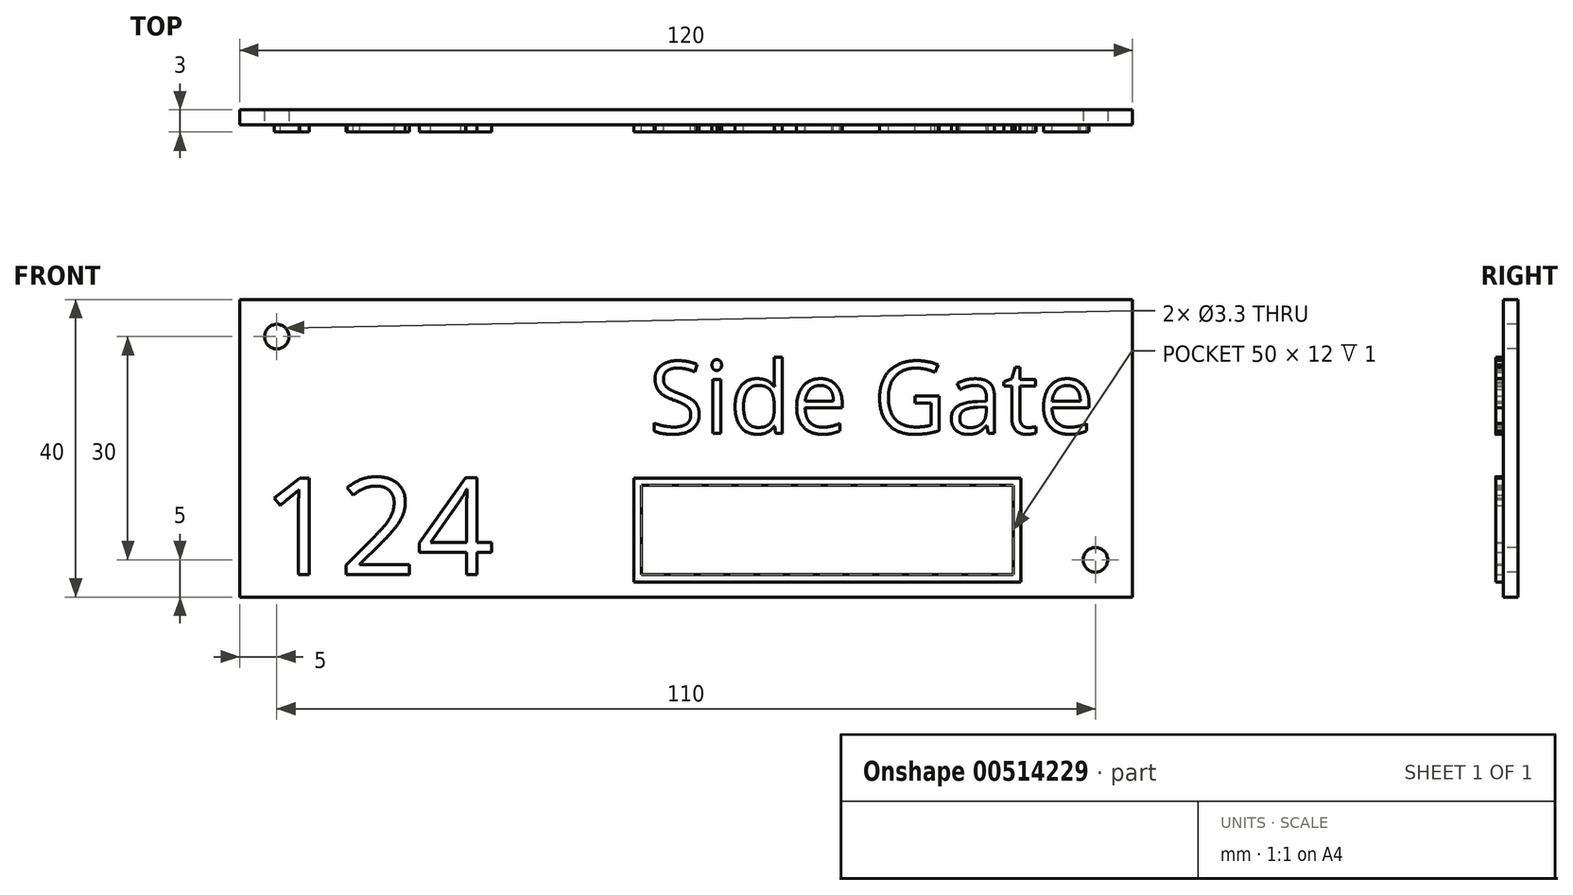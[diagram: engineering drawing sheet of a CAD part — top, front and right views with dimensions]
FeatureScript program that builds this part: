
annotation { "Feature Type Name" : "Feature", "Feature Type Description" : "" }
export const myFeature = defineFeature(function(context is Context, id is Id, definition is map)
    precondition{}
    {
        {
            var Q0;
            Q0=qCreatedBy(makeId("Front.planeOp"),FACE);
            var sketch = newSketch(context, id + "F0", { "sketchPlane" : qUnion([Q0])});
            skLineSegment(sketch, "E0.bottom", {"start": v(60, -20) * mm, "end": v(-60, -20) * mm});
            skLineSegment(sketch, "E0.top", {"start": v(60, 20) * mm, "end": v(-60, 20) * mm});
            skLineSegment(sketch, "E0.left", {"start": v(60, -20) * mm, "end": v(60, 20) * mm});
            skLineSegment(sketch, "E0.right", {"start": v(-60, -20) * mm, "end": v(-60, 20) * mm});
            skPoint(sketch, "E0.middle", {"position": v(0, 0) * mm});
            skSolve(sketch);
        }
        {
            var Q0;
            Q0=makeQuery(id+"F0.imprint","IMPRINT",FACE,{"disambiguationData":[TD([[makeQuery(id+"F0.imprint","IMPRINT",EDGE,{"derivedFrom":sQuery(id+"F0.wireOp",EDGE,"E0.bottom")}),-1.0]])]});
            extrude(context, id + "F1", {"entities" : qUnion([Q0]), "depth" : 2 * mm});
        }
        {
            var Q0;
            Q0=makeQuery(id+"F1.opExtrude","CAP_FACE",FACE,{"disambiguationData":[OSD([sQuery(id+"F0.wireOp",EDGE,"E0.bottom"),sQuery(id+"F0.wireOp",EDGE,"E0.top"),sQuery(id+"F0.wireOp",EDGE,"E0.left"),sQuery(id+"F0.wireOp",EDGE,"E0.right")])],"isStart":false});
            var sketch = newSketch(context, id + "F2", { "sketchPlane" : qUnion([Q0])});
            skPoint(sketch, "E1", {"position": v(-55, 15) * mm});
            skPoint(sketch, "E2", {"position": v(55, -15) * mm});
            skSolve(sketch);
        }
        {
            var Q0;
            Q0=sQuery(id+"F2.wireOp",VERTEX,"E1");
            var Q1;
            Q1=sQuery(id+"F2.wireOp",VERTEX,"E2");
            var Q2;
            Q2=makeQuery(id+"F1.opExtrude","SWEPT_BODY",BODY,{"disambiguationData":[OSD([sQuery(id+"F0.wireOp",EDGE,"E0.bottom"),sQuery(id+"F0.wireOp",EDGE,"E0.top"),sQuery(id+"F0.wireOp",EDGE,"E0.left"),sQuery(id+"F0.wireOp",EDGE,"E0.right")])]});
            hole(context, id + "F3", {"style" : HoleStyle.SIMPLE, "endStyle" : HoleEndStyle.THROUGH, "holeDiameter" : 3.3 * mm, "locations" : qUnion([Q0, Q1]), "scope" : qUnion([Q2]), "isTappedThrough" : true});
        }
        {
            var Q0;
            Q0=makeQuery(id+"F1.opExtrude","CAP_FACE",FACE,{"disambiguationData":[OSD([sQuery(id+"F0.wireOp",EDGE,"E0.bottom"),sQuery(id+"F0.wireOp",EDGE,"E0.top"),sQuery(id+"F0.wireOp",EDGE,"E0.left"),sQuery(id+"F0.wireOp",EDGE,"E0.right")])],"isStart":false});
            var sketch = newSketch(context, id + "F4", { "sketchPlane" : qUnion([Q0])});
            skText(sketch, "E3", { "text": "Side Gate", "fontName": "OpenSans-Regular.ttf"});
            const initialGuessF4  = {"E3": [-0.005, 0.002, 1, 0, 0.00972]};
            skSetInitialGuess(sketch, initialGuessF4);
            skSolve(sketch);
        }
        {
            var Q0;
            Q0=qSketchRegion(id+"F4",true);
            extrude(context, id + "F5", {"entities" : qUnion([Q0]), "operationType" : NewBodyOperationType.ADD, "depth" : 1 * mm});
        }
        {
            var Q0;
            {var subQ0=sQuery(id+"F0.wireOp",EDGE,"E0.top");var subQ1=sQuery(id+"F0.wireOp",EDGE,"E0.left");var subQ2=sQuery(id+"F0.wireOp",EDGE,"E0.right");var subQ3=sQuery(id+"F0.wireOp",EDGE,"E0.bottom");Q0=makeQuery(id+"F5.boolean.opBoolean","SPLIT",FACE,{"disambiguationData":[TD([makeQuery(id+"F1.opExtrude","SWEPT_FACE",FACE,{"disambiguationData":[OSD([subQ3])]})])],"derivedFrom":makeQuery(id+"F1.opExtrude","CAP_FACE",FACE,{"disambiguationData":[OSD([subQ3,subQ0,subQ1,subQ2])],"isStart":false})});}
            var sketch = newSketch(context, id + "F6", { "sketchPlane" : qUnion([Q0])});
            skText(sketch, "E4", { "text": "124", "fontName": "OpenSans-Regular.ttf"});
            const initialGuessF6  = {"E4": [-0.057, -0.017, 1, 0, 0.0131]};
            skSetInitialGuess(sketch, initialGuessF6);
            skSolve(sketch);
        }
        {
            var Q0;
            Q0=qSketchRegion(id+"F6",true);
            extrude(context, id + "F7", {"entities" : qUnion([Q0]), "operationType" : NewBodyOperationType.ADD, "depth" : 1 * mm});
        }
        {
            var Q0;
            {var subQ46=sQuery(id+"F0.wireOp",EDGE,"E0.top");var subQ48=sQuery(id+"F0.wireOp",EDGE,"E0.left");var subQ66=sQuery(id+"F0.wireOp",EDGE,"E0.right");var subQ76=sQuery(id+"F0.wireOp",EDGE,"E0.bottom");var subQ77=makeQuery(id+"F1.opExtrude","SWEPT_FACE",FACE,{"disambiguationData":[OSD([subQ76])]});Q0=makeQuery(id+"F7.boolean.opBoolean","SPLIT",FACE,{"disambiguationData":[TD([subQ77])],"derivedFrom":makeQuery(id+"F5.boolean.opBoolean","SPLIT",FACE,{"disambiguationData":[TD([subQ77])],"derivedFrom":makeQuery(id+"F1.opExtrude","CAP_FACE",FACE,{"disambiguationData":[OSD([subQ76,subQ46,subQ48,subQ66])],"isStart":false})})});}
            var sketch = newSketch(context, id + "F8", { "sketchPlane" : qUnion([Q0])});
            skLineSegment(sketch, "E5.bottom", {"start": v(45, -18) * mm, "end": v(-7, -18) * mm});
            skLineSegment(sketch, "E5.top", {"start": v(45, -4) * mm, "end": v(-7, -4) * mm});
            skLineSegment(sketch, "E5.left", {"start": v(45, -18) * mm, "end": v(45, -4) * mm});
            skLineSegment(sketch, "E5.right", {"start": v(-7, -18) * mm, "end": v(-7, -4) * mm});
            skPoint(sketch, "E5.middle", {"position": v(19, -11) * mm});
            skLineSegment(sketch, "E6.0", {"start": v(44, -5) * mm, "end": v(-6, -5) * mm});
            skLineSegment(sketch, "E6.1", {"start": v(44, -17) * mm, "end": v(44, -5) * mm});
            skLineSegment(sketch, "E6.2", {"start": v(44, -17) * mm, "end": v(-6, -17) * mm});
            skLineSegment(sketch, "E6.3", {"start": v(-6, -17) * mm, "end": v(-6, -5) * mm});
            skSolve(sketch);
        }
        {
            var Q0;
            Q0=makeQuery(id+"F8.imprint","IMPRINT",FACE,{"disambiguationData":[TD([[makeQuery(id+"F8.imprint","IMPRINT",EDGE,{"derivedFrom":sQuery(id+"F8.wireOp",EDGE,"E5.bottom")}),-1.0]])]});
            extrude(context, id + "F9", {"entities" : qUnion([Q0]), "operationType" : NewBodyOperationType.ADD, "depth" : 1 * mm});
        }
    });
